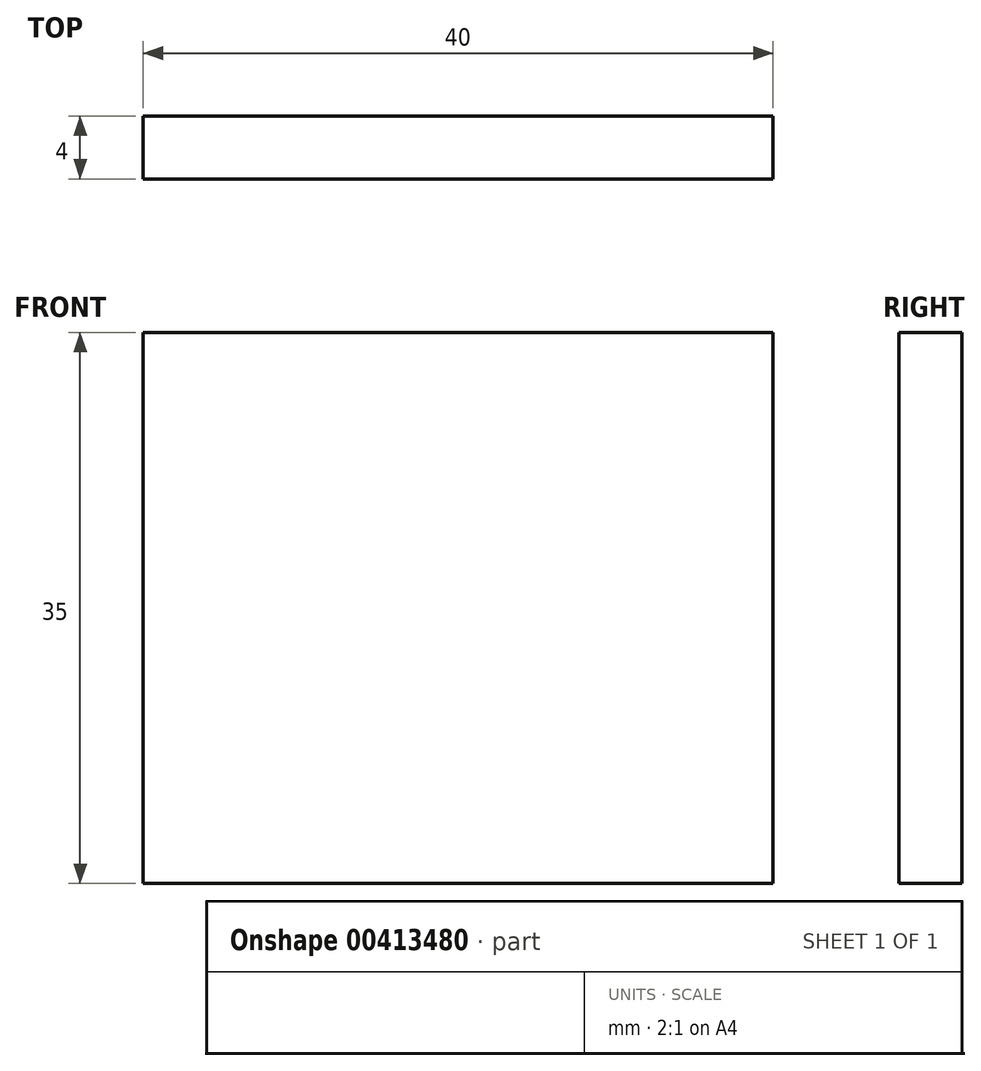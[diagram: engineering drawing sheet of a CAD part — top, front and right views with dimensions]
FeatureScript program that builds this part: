
annotation { "Feature Type Name" : "Feature", "Feature Type Description" : "" }
export const myFeature = defineFeature(function(context is Context, id is Id, definition is map)
    precondition{}
    {
        {
            var Q0;
            Q0=qCreatedBy(makeId("Front.planeOp"),FACE);
            var sketch = newSketch(context, id + "F0", { "sketchPlane" : qUnion([Q0])});
            skLineSegment(sketch, "E0.bottom", {"start": v(-20, 0) * mm, "end": v(20, 0) * mm});
            skLineSegment(sketch, "E0.top", {"start": v(-20, -35) * mm, "end": v(20, -35) * mm});
            skLineSegment(sketch, "E0.left", {"start": v(-20, 0) * mm, "end": v(-20, -35) * mm});
            skLineSegment(sketch, "E0.right", {"start": v(20, 0) * mm, "end": v(20, -35) * mm});
            skSolve(sketch);
        }
        {
            var Q0;
            Q0=qSketchRegion(id+"F0",true);
            extrude(context, id + "F1", {"entities" : qUnion([Q0]), "depth" : 4 * mm});
        }
    });
